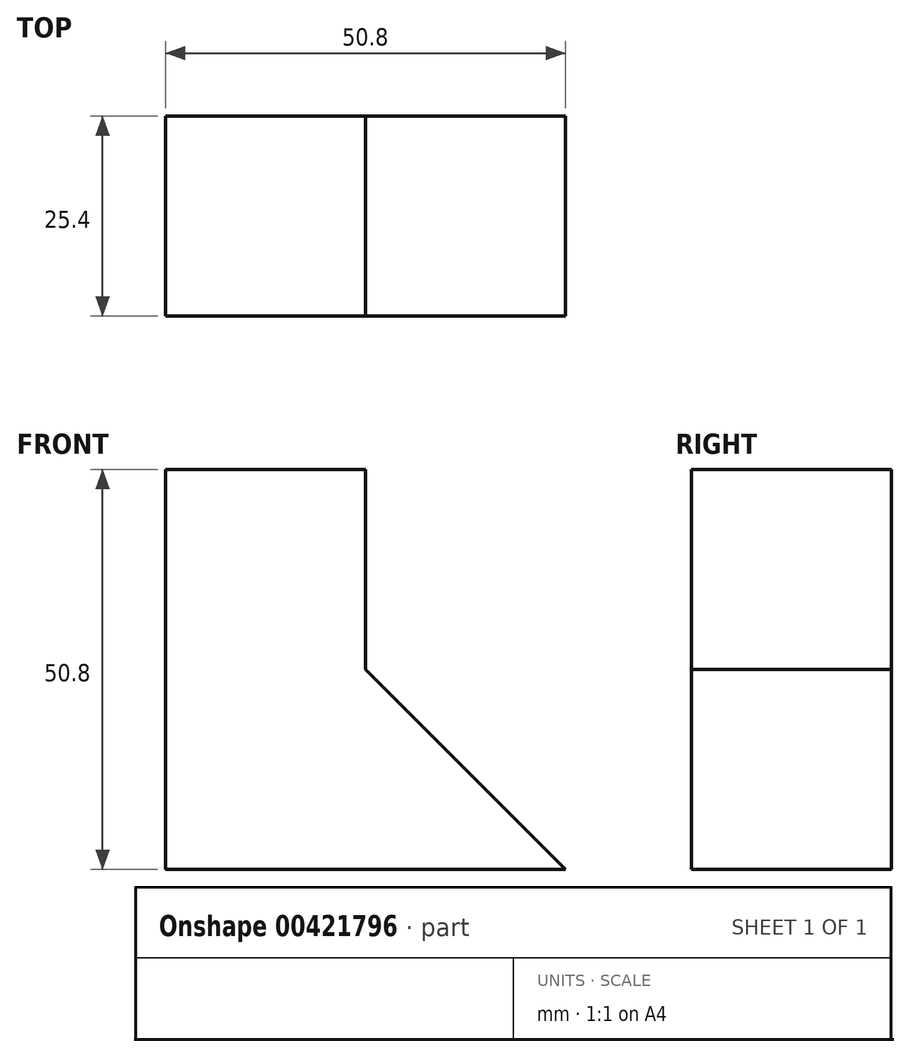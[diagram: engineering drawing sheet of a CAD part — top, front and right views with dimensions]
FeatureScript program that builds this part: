
annotation { "Feature Type Name" : "Feature", "Feature Type Description" : "" }
export const myFeature = defineFeature(function(context is Context, id is Id, definition is map)
    precondition{}
    {
        {
            var Q0;
            Q0=qCreatedBy(makeId("Front.planeOp"),FACE);
            var sketch = newSketch(context, id + "F0", { "sketchPlane" : qUnion([Q0])});
            skLineSegment(sketch, "E0", {"start": v(0, 50.8) * mm, "end": v(0, 0) * mm});
            skLineSegment(sketch, "E1", {"start": v(0, 0) * mm, "end": v(50.8, 0) * mm});
            skLineSegment(sketch, "E2", {"start": v(0, 50.8) * mm, "end": v(25.4, 50.8) * mm});
            skLineSegment(sketch, "E3", {"start": v(25.4, 50.8) * mm, "end": v(25.4, 25.4) * mm});
            skLineSegment(sketch, "E4", {"start": v(25.4, 25.4) * mm, "end": v(50.8, 0) * mm});
            skSolve(sketch);
        }
        {
            var Q0;
            Q0 = qSketchRegion(id + "F0", true);
            extrude(context, id + "F1", {"entities" : qUnion([Q0]), "depth" : 25.4 * mm});
        }
    });
